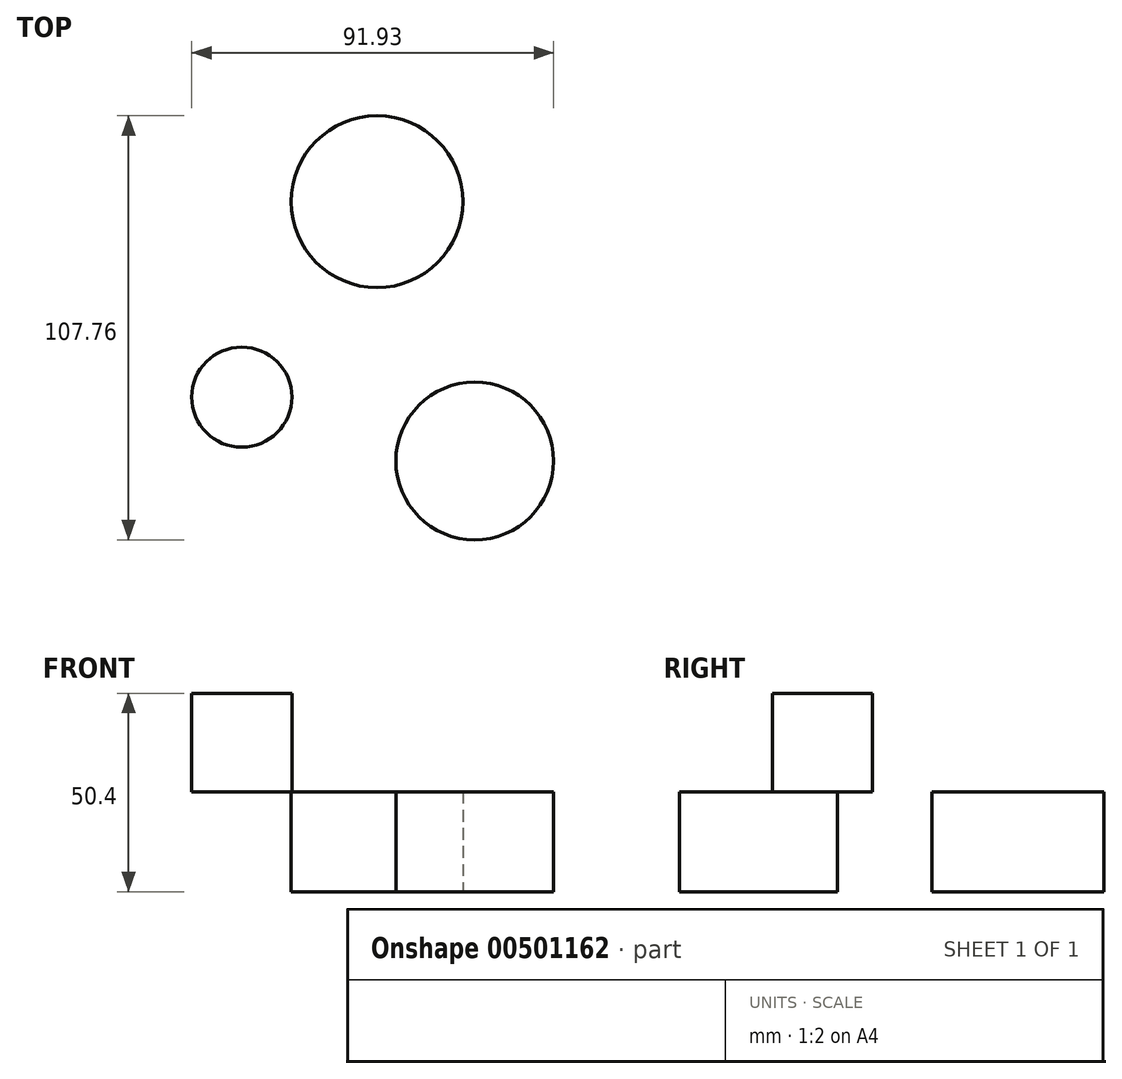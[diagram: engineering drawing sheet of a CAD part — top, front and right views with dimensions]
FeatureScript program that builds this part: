
annotation { "Feature Type Name" : "Feature", "Feature Type Description" : "" }
export const myFeature = defineFeature(function(context is Context, id is Id, definition is map)
    precondition{}
    {
        {
            var Q0;
            Q0=qCreatedBy(makeId("Top.planeOp"),FACE);
            var sketch = newSketch(context, id + "F0", { "sketchPlane" : qUnion([Q0])});
            skCircle(sketch, "E0", {"center": v(0, 0) * mm, "radius": 20.04 * mm});
            skCircle(sketch, "E1", {"center": v(-24.82, 65.9) * mm, "radius": 21.83 * mm});
            skSolve(sketch);
        }
        {
            var Q0;
            Q0 = qSketchRegion(id + "F0", true);
            extrude(context, id + "F1", {"entities" : qUnion([Q0]), "depth" : 25.4 * mm});
        }
        {
            var Q0;
            Q0=makeQuery(id+"F1.opExtrude","CAP_FACE",FACE,{"disambiguationData":[OSD([sQuery(id+"F0.wireOp",EDGE,"E1")])],"isStart":false});
            var sketch = newSketch(context, id + "F2", { "sketchPlane" : qUnion([Q0])});
            skCircle(sketch, "E2", {"center": v(-59.17, 16.23) * mm, "radius": 12.72 * mm});
            skSolve(sketch);
        }
        {
            var Q0;
            Q0 = qSketchRegion(id + "F2", true);
            extrude(context, id + "F3", {"entities" : qUnion([Q0]), "depth" : 25 * mm});
        }
    });
